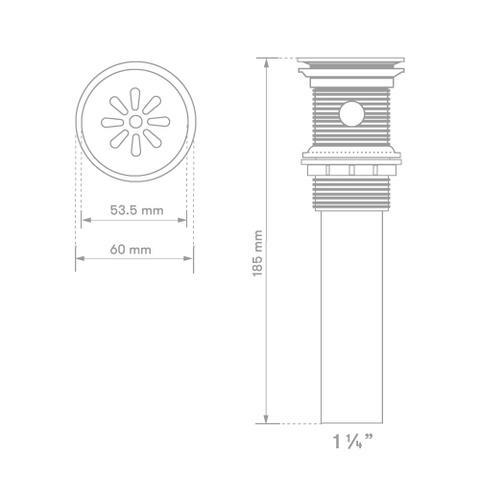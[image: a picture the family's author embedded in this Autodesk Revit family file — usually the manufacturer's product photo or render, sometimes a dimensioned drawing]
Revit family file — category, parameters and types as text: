
# Revit family: DESAGÜE PUSH LARGO SIN REBOSE
name_source: partatom
category: Aparatos sanitarios
units: mm (PartAtom-declared; Revit-internal decimal feet)

## family parameters
Compartido = No
Corte con vacíos al cargar = No
Cota de conector redondo = Diámetro de uso
Número OmniClass = 23.45.00.00
Punto de cálculo de habitación = No
Se basa en plano de trabajo = No
Siempre vertical = Sí
Tipo de pieza = Normal
Título OmniClass = Sanitary, Laundry, and Cleaning Equipment

## types (1)
- DESAGÜE PUSH LARGO SIN REBOSE
    Caucho = Caucho
    Conexión AC = No
    Conexión AF = No
    Conexión de residuos = No
    Conexión de ventilación = No
    Costo = 0 $
    Elevación por defecto = 0 mm  [stored 0 ft]
    Metal Laton Cromado = Metal Laton Cromado
    Nominal height = 130
    Nominal width = 370
    Plastico - ABS Cromado = Plastico - ABS Cromado
    Weight Net (Kg) = 6.60Kg

note: [stored X ft] marks values corroborated as IEEE doubles in the binary element streams (Revit-internal decimal feet)

## geometry (parser evidence)
native form markers: Blend x2, Sweep x1
no freeform markers — native parametric forms only
